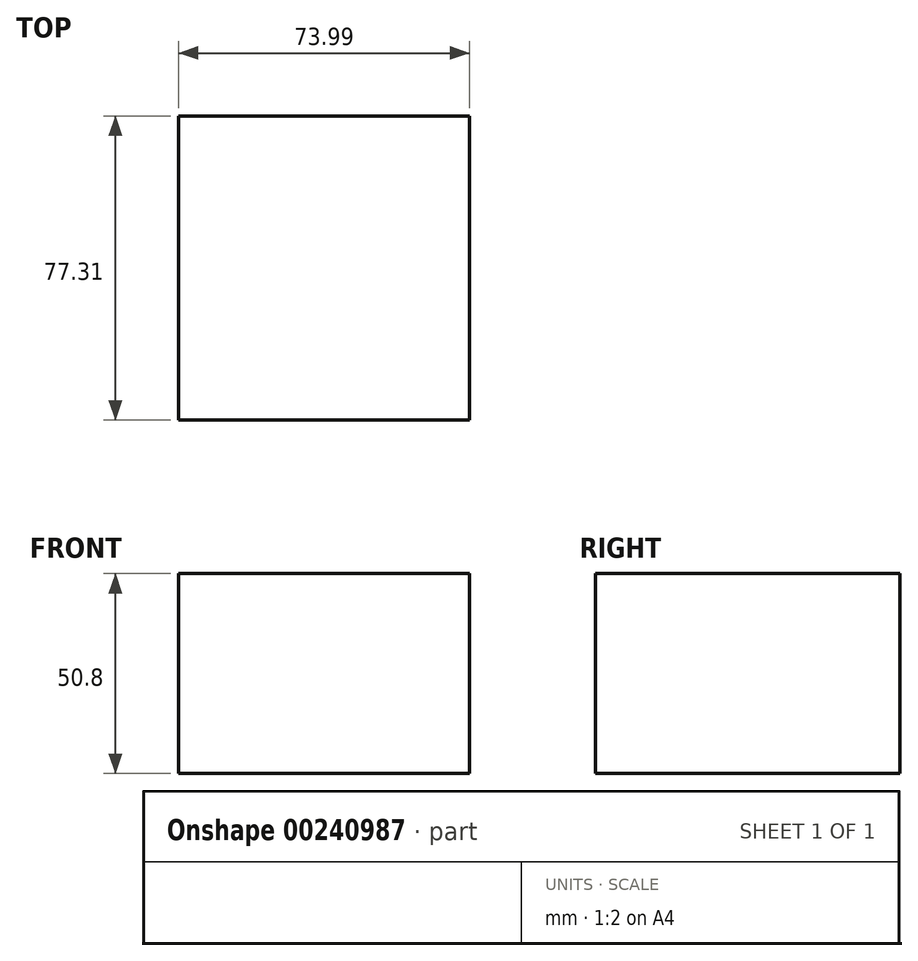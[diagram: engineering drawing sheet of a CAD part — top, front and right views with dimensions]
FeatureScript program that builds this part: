
annotation { "Feature Type Name" : "Feature", "Feature Type Description" : "" }
export const myFeature = defineFeature(function(context is Context, id is Id, definition is map)
    precondition{}
    {
        {
            var Q0;
            Q0=qCreatedBy(makeId("Top.planeOp"),FACE);
            var sketch = newSketch(context, id + "F0", { "sketchPlane" : qUnion([Q0])});
            skLineSegment(sketch, "E0.bottom", {"start": v(-30.95, 21.04) * mm, "end": v(43.04, 21.04) * mm});
            skLineSegment(sketch, "E0.top", {"start": v(-30.95, -56.27) * mm, "end": v(43.04, -56.27) * mm});
            skLineSegment(sketch, "E0.left", {"start": v(-30.95, 21.04) * mm, "end": v(-30.95, -56.27) * mm});
            skLineSegment(sketch, "E0.right", {"start": v(43.04, 21.04) * mm, "end": v(43.04, -56.27) * mm});
            skSolve(sketch);
        }
        {
            var Q0;
            Q0=makeQuery(id+"F0.imprint","IMPRINT",FACE,{"disambiguationData":[TD([[makeQuery(id+"F0.imprint","IMPRINT",EDGE,{"derivedFrom":sQuery(id+"F0.wireOp",EDGE,"E0.bottom")}),-1.0]])]});
            extrude(context, id + "F1", {"entities" : qUnion([Q0]), "depth" : 50.8 * mm});
        }
    });
